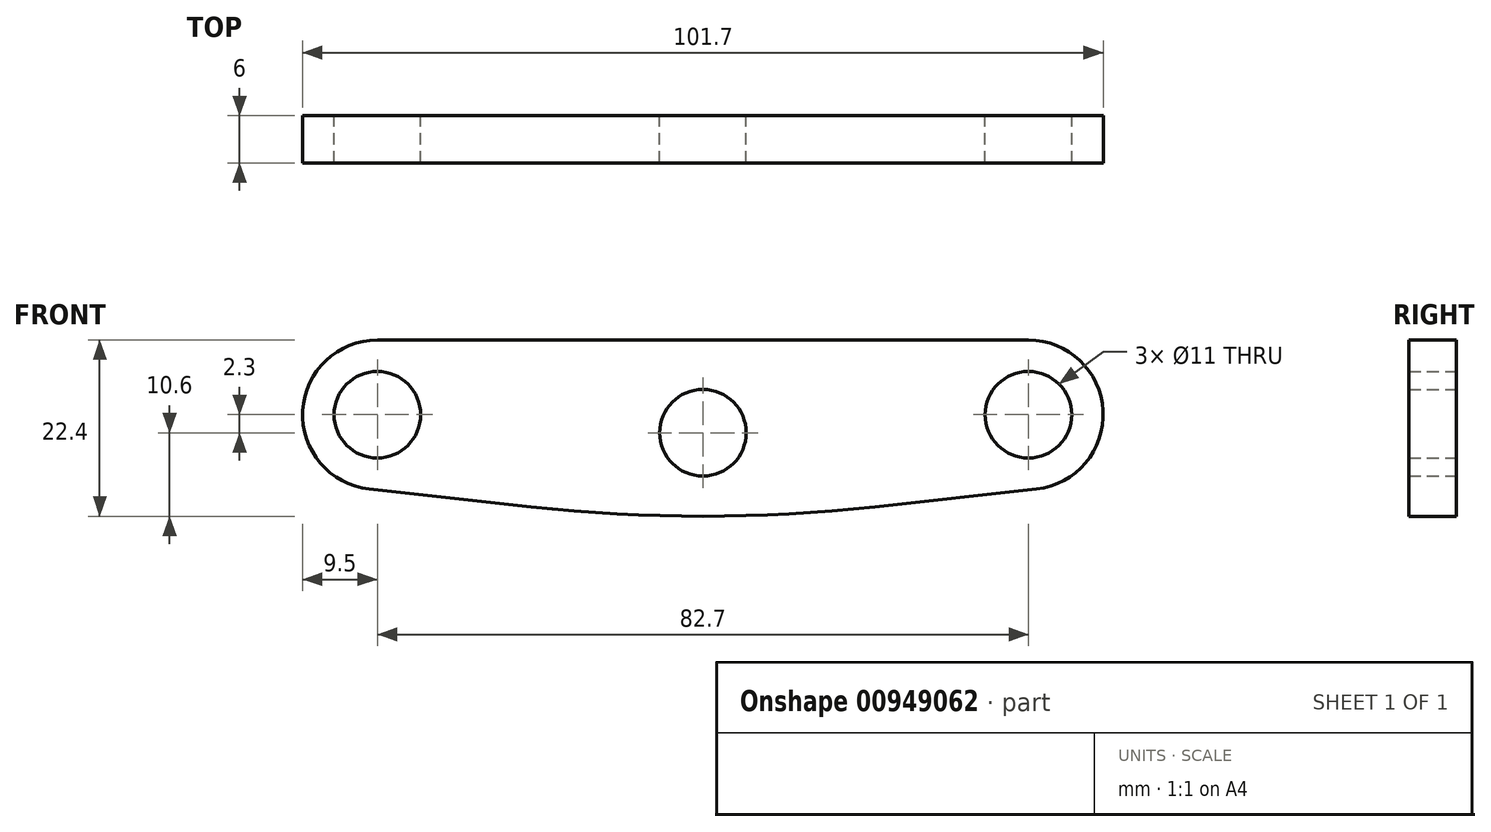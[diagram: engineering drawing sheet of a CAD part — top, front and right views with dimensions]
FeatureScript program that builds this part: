
annotation { "Feature Type Name" : "Feature", "Feature Type Description" : "" }
export const myFeature = defineFeature(function(context is Context, id is Id, definition is map)
    precondition{}
    {
        {
            var Q0;
            Q0=qCreatedBy(makeId("Front.planeOp"),FACE);
            var sketch = newSketch(context, id + "F0", { "sketchPlane" : qUnion([Q0])});
            skCircle(sketch, "E0", {"center": v(0, 0) * mm, "radius": 5.5 * mm});
            skCircle(sketch, "E1", {"center": v(-41.35, 2.3) * mm, "radius": 5.5 * mm});
            skCircle(sketch, "E2", {"center": v(41.35, 2.3) * mm, "radius": 5.5 * mm});
            skArc(sketch, "E3", {"start": v(-41.35, 11.8) * mm, "mid": v(-50.84, 2.82) * mm, "end": v(-42.39, -7.14) * mm});
            skCircle(sketch, "E4", {"center": v(0, 0) * mm, "radius": 11.8 * mm, "construction": true});
            skArc(sketch, "E5", {"start": v(42.39, -7.14) * mm, "mid": v(50.84, 2.82) * mm, "end": v(41.35, 11.8) * mm});
            skLineSegment(sketch, "E6", {"start": v(-42.39, -7.14) * mm, "end": v(0, -11.8) * mm});
            skLineSegment(sketch, "E7", {"start": v(0, -11.8) * mm, "end": v(42.39, -7.14) * mm});
            skLineSegment(sketch, "E8", {"start": v(-41.35, 11.8) * mm, "end": v(41.35, 11.8) * mm});
            skSolve(sketch);
        }
        {
            var Q0;
            Q0=makeQuery(id+"F0.imprint","IMPRINT",FACE,{"disambiguationData":[TD([[makeQuery(id+"F0.imprint","IMPRINT",EDGE,{"derivedFrom":sQuery(id+"F0.wireOp",EDGE,"E0")}),-1.0]])]});
            extrude(context, id + "F1", {"entities" : qUnion([Q0]), "depth" : 6 * mm, "offsetDistance" : 25 * mm});
        }
        {
            var Q0;
            Q0=makeQuery(id+"F1.opExtrude","SWEPT_EDGE",EDGE,{"disambiguationData":[OSD([sQuery(id+"F0.wireOp",EDGE,"E6"),sQuery(id+"F0.wireOp",EDGE,"E7")])]});
            fillet(context, id + "F2", {"entities" : qUnion([Q0]), "radius" : 200 * mm, "tangentPropagation" : true, "allowEdgeOverflow" : false});
        }
    });
